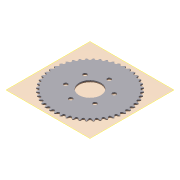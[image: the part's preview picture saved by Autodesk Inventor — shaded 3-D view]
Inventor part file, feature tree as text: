
AUTODESK INVENTOR PART (.ipt)
format: ipt  version: 2011 (Build 150239000, 239)  size: 1,133,568 bytes
history: native  units: mm
features: other x6, extrude x2, hole x2, sketch x2, pattern_linear x1, pattern_circular x1
ambient origin geometry x8: Origin, YZ Plane, XZ Plane, XY Plane, X Axis, Y Axis, Z Axis, Center Point
bodies: Solid1 (feature_tree)
feature tree (14):
  other  "Theoretical Tooth Profile"
  other  "Tooth Profile"
  other  "Section Profile"
  other  "Shroud"
  other  "Strand"
  pattern_linear  "Strand Pattern"  Spacing1=1.697355mm  [1 undecoded]
  extrude  "Theoretical Tooth"  Depth=22.034782mm
  extrude  "Tooth"  Depth=2.937971mm
  pattern_circular  "Tooth Pattern"  [2 undecoded]
  other  "Timing Plane"
  hole  "Hole1"  [1 undecoded]
  hole  "Hole2"  [1 undecoded]
  sketch  "Sketch4"  dims[d0=97.090156mm]
  sketch  "Sketch5"  dims[d2=1.308997mm d3=1.697355mm d10=22.034782mm d11=2.937971mm d12=2.6416mm d13=4.338955mm d14=4.6228mm d18=10.0mm d19=0.0mm d20=480.0mm d21=360.0deg d23=1.905mm d28=0.0mm d29=0.0mm d30=2.286mm d31=89.262278mm d32=2.286mm d33=0.79375mm d34=6.75005mm d36=90.0deg d37=90.0deg d38=10.0mm d40=6.4008mm d42=0.0mm d43=1.143mm d44=24.107361mm d45=1.697355mm d46=19.812mm d47=0.0mm d48=25.4mm d49=0.0mm d50=10.0mm d51=28.5623mm d52=28.5623mm d53=19.05mm d54=9.525mm d55=6.35mm d56=14.3117mm d57=25.4mm d58=20.594885mm d59=47.625mm d60=5.2324mm d61=60.0mm d63=360.0deg d65=5.2324mm d66=19.05mm d67=9.525mm d68=6.35mm d69=14.3117mm d70=25.4mm d71=20.594885mm]
note: 5 required parameter values undecoded (feature->parameter linkage not recoverable at this tier; creation-order binding heuristic only, values carry confidence <= 0.55)
